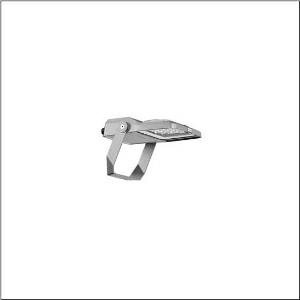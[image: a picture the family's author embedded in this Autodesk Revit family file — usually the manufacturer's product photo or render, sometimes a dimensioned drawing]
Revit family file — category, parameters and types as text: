
# Revit family: floodlight_fl_21_iq_micro___rs12_5xa7762a2b1a_2903
name_source: partatom
category: Lighting Fixtures
units: mm (PartAtom-declared; Revit-internal decimal feet)

## family parameters
Cut with Voids When Loaded = No
Host = Face
Light Source = No
Part Type = Normal
Room Calculation Point = No
Round Connector Dimension = Use Diameter
Shared = No

## types (1)
- --- (1 x LED, 3090 lm, 23.1 W, 3000K)
    Apparent Load = 23 VA
    CIE Flux Codes = 79 92 99 100 100
    Color Rendering = 70
    Color Temperature = 3000K
    Default Elevation = 1800 mm
    Description = Floodlight FL 21 iQ micro, floodlight, primary light control with lens, of PMMA, primary optical cover: protective disc, of toughened safety glass, transparent, light distribution: RS12, light emission: direct distribution, installation type: surface-mounted, LED, High Power LED, rated luminous flux: 3.090lm, luminous efficacy: 134lm/W, light colour: 730, colour temperature: 3000K, control gear: iQ Street-Remote/DALI, control: Auto-Match, Temp-Guard, Night-Set, Smart-Wire, Desk-Remote (wireless, voltage-free reading and setting of iQ features in the workshop via application-optimized NFC function/RFID function), optimised constant luminous flux control (CLO 2.0), Street-Remote, with terminal, 6-pole, mains connection: 220..240V, AC, 50/60Hz, start of lifetime: 23W, end of service life: 24W, reduction: 11W, luminaire housing, of diecast aluminium, powder-coated, Siteco® metallic grey (DB 702S), corrosivity category C5 mid according to DIN EN ISO 12944, suitable for swimming pools, chlorine-resistant, sealing non-destructively replaceable, mounting bracket, of steel, galvanised, powder-coated, Siteco® metallic grey (DB 702S), protection rating (complete): IP66, insulation class (complete): insulation class II (safety insulation), certification: CE, ENEC, VDE, protection symbol: D, impact resistance: IK07, permissible operating ambient temperature: -40..+40°C, permissible operating ambient temperature for outdoor applications: -40..+50°C, standard: DIN EN 12944, LABS conformity tested according to VDMA 24364:2018-05, packaging unit: 1 piece

Light Distribution: RS12
    Height = 65 mm
    Lamp = 1 x LED
    Lamp Light Flux = 3090 lm
    Lamp Power = 23.1 W
    Lamp count = 1
    Length = 312 mm
    Luminous efficacy = 134 lm/W
    Manufacturer = Siteco
    ModVariant = No
    Model = 5XA7762A2B1A
    Number of Poles = 1
    OnlyDefault = Yes
    Power Factor = 1
    Product Name = Floodlight FL 21 iQ micro | RS12
    Product group = floodlight | pylon annexe
    ProductGroupID = 6200
    Protection Class = Protection class II
    Protection Degree = IP 66
    RLX_Detail_Level = 1
    RLX_Emergency_Light_Flux = 0 lm
    RLX_Emergency_Type = 0
    RLX_Emergency_Type_DB = No
    RlxData = <blob elided: 75085 chars, md5=00fc7a5d>
    Socket = socket
    Standby Power = 0 W
    System Light Flux = 3090 lm
    System Power = 23 W
    Type Comments = factory setting: luminous flux: 100 % | dim-lin: 254 | 455 mA
    Type Image = l_1006880.jpg
    URL = http://relux.com
    VarID = @adj_181822
    Voltage = 0 V
    Weight = 0.00 kg
    Width = 230 mm

## geometry (parser evidence)
native form markers: Blend x4, Sweep x12
no freeform markers — native parametric forms only
